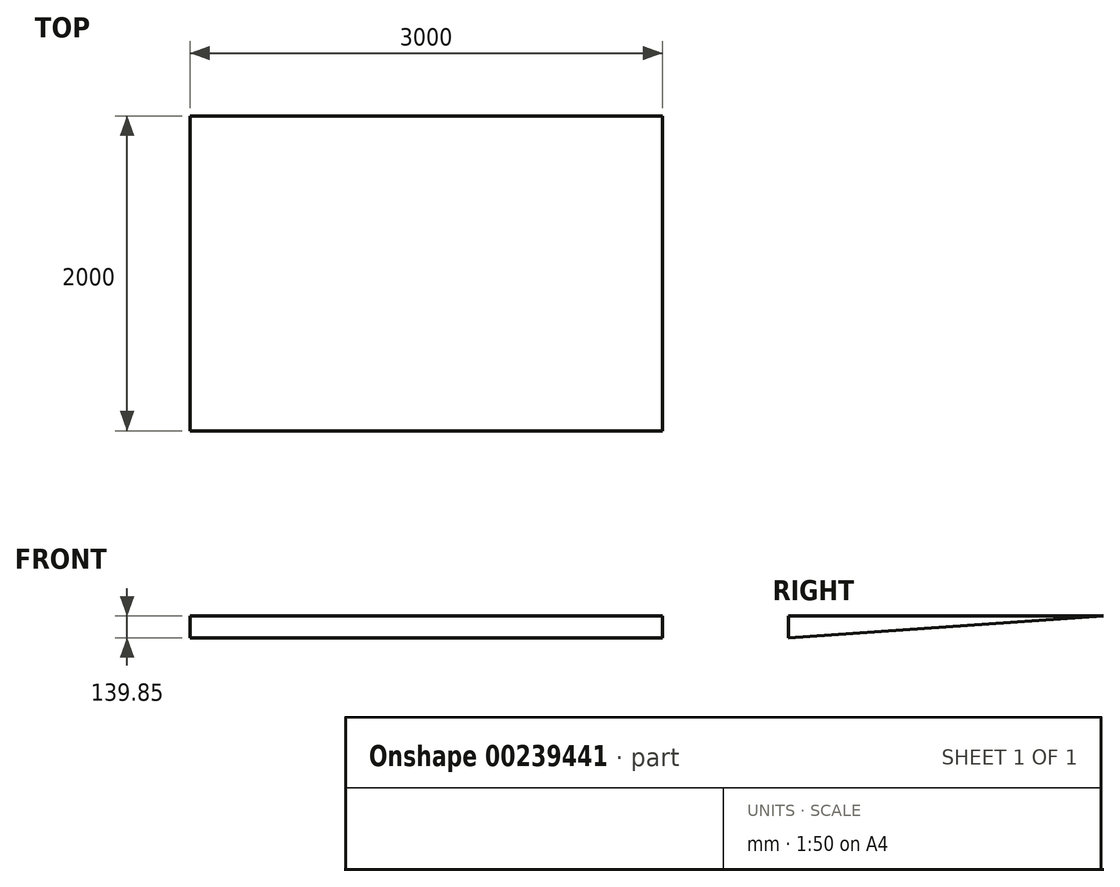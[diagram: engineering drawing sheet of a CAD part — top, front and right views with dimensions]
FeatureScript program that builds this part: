
annotation { "Feature Type Name" : "Feature", "Feature Type Description" : "" }
export const myFeature = defineFeature(function(context is Context, id is Id, definition is map)
    precondition{}
    {
        {
            var Q0;
            Q0=qCreatedBy(makeId("Right.planeOp"),FACE);
            var sketch = newSketch(context, id + "F0", { "sketchPlane" : qUnion([Q0])});
            skLineSegment(sketch, "E0", {"start": v(0, 0) * mm, "end": v(237.72, 509.8) * mm, "construction": true});
            skLineSegment(sketch, "E1", {"start": v(237.72, 509.8) * mm, "end": v(68.06, 588.91) * mm, "construction": true});
            skLineSegment(sketch, "E2", {"start": v(68.06, 588.91) * mm, "end": v(-1931.94, 449.06) * mm});
            skLineSegment(sketch, "E3", {"start": v(-1931.94, 449.06) * mm, "end": v(-1931.94, 588.91) * mm});
            skLineSegment(sketch, "E4", {"start": v(-1931.94, 588.91) * mm, "end": v(68.06, 588.91) * mm});
            skLineSegment(sketch, "E5", {"start": v(0, 0) * mm, "end": v(0, 471.56) * mm, "construction": true});
            skSolve(sketch);
        }
        {
            var Q0;
            Q0 = qSketchRegion(id + "F0", true);
            extrude(context, id + "F1", {"entities" : qUnion([Q0]), "depth" : 1500 * mm, "hasSecondDirection" : true, "secondDirectionOppositeDirection" : true, "secondDirectionDepth" : 1500 * mm});
        }
    });
